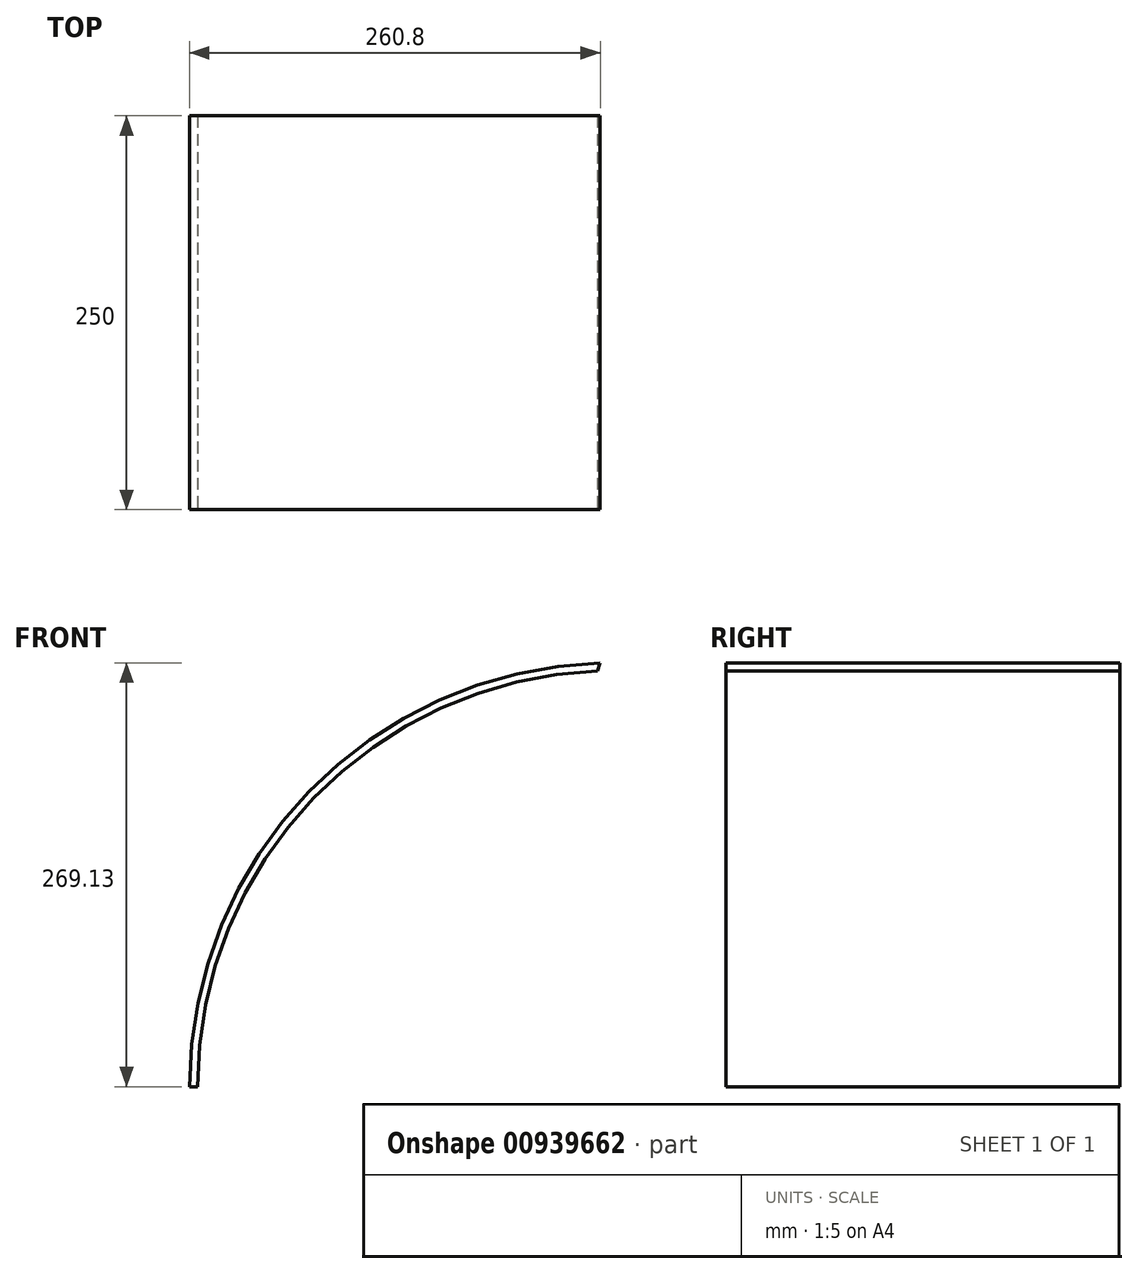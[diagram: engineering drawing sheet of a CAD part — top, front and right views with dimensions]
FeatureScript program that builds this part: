
annotation { "Feature Type Name" : "Feature", "Feature Type Description" : "" }
export const myFeature = defineFeature(function(context is Context, id is Id, definition is map)
    precondition{}
    {
        {
            var Q0;
            Q0=qCreatedBy(makeId("Front.planeOp"),FACE);
            var sketch = newSketch(context, id + "F0", { "sketchPlane" : qUnion([Q0])});
            skArc(sketch, "E0", {"start": v(241.54, 269.13) * mm, "mid": v(56.64, 187.38) * mm, "end": v(-19.26, 0) * mm});
            skLineSegment(sketch, "E1.bottom", {"start": v(-19.26, 0) * mm, "end": v(-14.26, 0) * mm});
            skArc(sketch, "E2", {"start": v(-14.26, 0) * mm, "mid": v(59.62, 183.27) * mm, "end": v(239.94, 264.07) * mm});
            skLineSegment(sketch, "E3", {"start": v(239.94, 264.07) * mm, "end": v(241.54, 269.13) * mm});
            skSolve(sketch);
        }
        {
            var Q0;
            Q0=qSketchRegion(id+"F0",true);
            extrude(context, id + "F1", {"entities" : qUnion([Q0]), "oppositeDirection" : true, "depth" : 6 * mm, "offsetDistance" : 25 * mm});
        }
        {
            var Q0;
            Q0 = qSketchRegion(id + "F0", true);
            var Q1;
            Q1=makeQuery(id+"F1.opExtrude","CAP_FACE",FACE,{"disambiguationData":[OSD([sQuery(id+"F0.wireOp",EDGE,"E0"),sQuery(id+"F0.wireOp",EDGE,"E2"),sQuery(id+"F0.wireOp",EDGE,"E3"),sQuery(id+"F0.wireOp",EDGE,"E1.bottom")])],"isStart":true});
            extrude(context, id + "F2", {"entities" : qUnion([Q0, Q1]), "operationType" : NewBodyOperationType.ADD, "oppositeDirection" : true, "depth" : 250 * mm, "offsetDistance" : 25 * mm});
        }
    });
